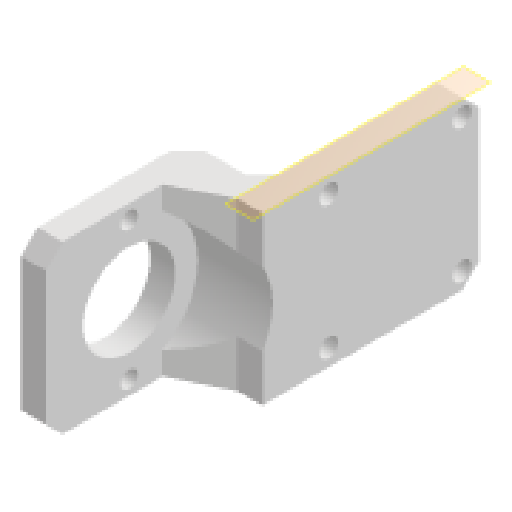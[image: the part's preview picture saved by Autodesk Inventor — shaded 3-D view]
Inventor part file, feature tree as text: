
AUTODESK INVENTOR PART (.ipt)
format: ipt  version: 2024.1 (Build 281209000, 209)  size: 175,104 bytes
history: native  units: mm
features: extrude x5, sketch x5, projected_geometry x4, plane x1, chamfer x1
ambient origin geometry x8: Origin, YZ Plane, XZ Plane, XY Plane, X Axis, Y Axis, Z Axis, Center Point
bodies: Volumenkörper1 (feature_tree)
feature tree (16):
  extrude  "Extrusion1"  Depth=40.0mm
  plane  "Arbeitsebene1"
  extrude  "Extrusion2"  Depth=32.0mm
  chamfer  "Fasen1"  Distance=4.5mm
  extrude  "Extrusion3"  Depth=12.0mm
  extrude  "Extrusion4"  Depth=6.0mm TaperAngle=0.0deg
  extrude  "Extrusion5"  TaperAngle=0.0deg  [1 undecoded]
  sketch  "Skizze1"  dims[d0=40.0mm d1=40.0mm]
  sketch  "Skizze2"  dims[d2=32.0mm d3=32.0mm]
  projected_geometry  "Projizierte Kontur1"
  sketch  "Skizze3"  dims[d4=4.5mm]
  projected_geometry  "Projizierte Kontur2"
  sketch  "Skizze4"  dims[d5=4.5mm]
  projected_geometry  "Projizierte Kontur3"
  sketch  "Skizze5"  dims[d6=4.5mm d7=4.5mm d8=12.0mm d9=6.0mm d10=0.0mm d11=0.0mm d12=6.0mm d13=45.0mm d14=6.0mm d15=12.0mm d16=12.0mm d17=6.0mm d18=0.0mm d19=4.0mm d20=2.0mm d21=45.0deg d22=33.0mm d23=0.0mm d24=0.0mm d25=4.0mm d26=4.0mm d27=10.0mm d28=0.0mm d29=22.0mm d30=10.0mm d31=0.0mm]
  projected_geometry  "Projizierte Kontur4"
note: 1 required parameter value undecoded (feature->parameter linkage not recoverable at this tier; creation-order binding heuristic only, values carry confidence <= 0.55)
